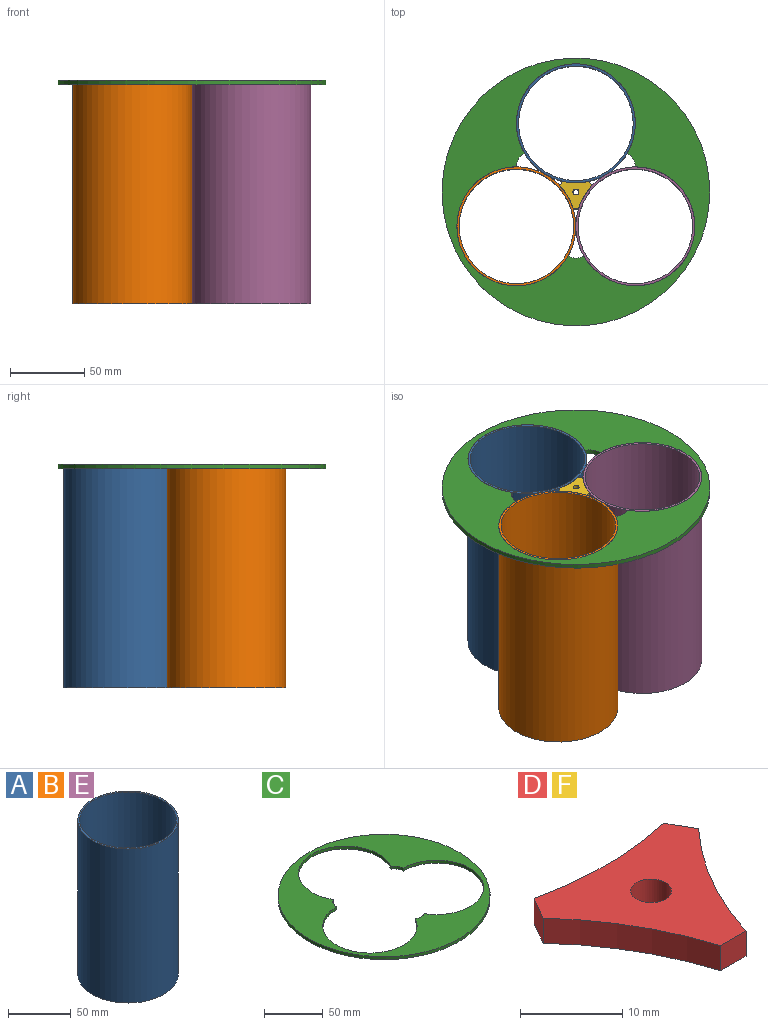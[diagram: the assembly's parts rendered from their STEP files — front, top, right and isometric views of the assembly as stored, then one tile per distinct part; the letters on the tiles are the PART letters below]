
ASSEMBLY  parts=6 mates=11
PART A: 4 faces, bbox 80x80x150 mm
  f0: cylinder r=38.5mm len=150mm, axis (0,0,-1), area 36285.4mm2, adj f2,f3
  f1: cylinder r=40mm len=150mm, axis (0,0,-1), area 37699.1mm2, adj f2,f3
  f2: plane 80x80mm, normal (0,0,1), area 369.9mm2, adj f0,f1
  f3: plane 80x80mm, normal (0,0,-1), area 369.9mm2, adj f0,f1
PART B: same geometry as A
PART C: 9 faces, bbox 180x180x3 mm
  f0: cylinder r=40mm len=80mm, axis (0,0,-1), area 502.7mm2, adj f1,f5,f7,f8
  f1: cylinder r=10.72mm len=9.28mm, axis (0,0,-1), area 33.7mm2, adj f0,f2,f7,f8
  f2: cylinder r=40mm len=80mm, axis (0,0,-1), area 502.7mm2, adj f1,f3,f7,f8
  f3: cylinder r=10.72mm len=10.72mm, axis (0,0,-1), area 33.7mm2, adj f2,f4,f7,f8
  f4: cylinder r=40mm len=80mm, axis (0,0,-1), area 502.7mm2, adj f3,f5,f7,f8
  f5: cylinder r=10.72mm len=9.28mm, axis (0,0,-1), area 33.7mm2, adj f0,f4,f7,f8
  f6: cylinder r=90mm len=180mm, axis (0,0,-1), area 1696.5mm2, adj f7,f8
  f7: plane 180x180mm, normal (0,0,1), area 9869.8mm2, adj f0,f1,f2,f3,f4,f5,f6
  f8: plane 180x180mm, normal (0,0,-1), area 9869.8mm2, adj f0,f1,f2,f3,f4,f5,f6
PART D: 9 faces, bbox 21.5x18.6x3 mm
  f0: plane 3.03x3mm, normal (-0.87,0.5,0), area 10.5mm2, adj f1,f5,f7,f8
  f1: cylinder r=40mm len=15.57mm, axis (0,0,-1), area 54.4mm2, adj f0,f2,f7,f8
  f2: plane 3.5x3mm, normal (0,-1,0), area 10.5mm2, adj f1,f3,f7,f8
  f3: cylinder r=40mm len=15.57mm, axis (0,0,-1), area 54.4mm2, adj f2,f4,f7,f8
  f4: plane 3.03x3mm, normal (0.87,0.5,0), area 10.5mm2, adj f3,f5,f7,f8
  f5: cylinder r=40mm len=17.98mm, axis (0,0,-1), area 54.4mm2, adj f0,f4,f7,f8
  f6: cylinder r=2mm len=4mm, axis (0,0,-1), area 37.7mm2, adj f7,f8
  f7: plane 21.48x18.6mm, normal (0,0,1), area 204.8mm2, adj f0,f1,f2,f3,f4,f5,f6
  f8: plane 21.48x18.6mm, normal (0,0,-1), area 204.8mm2, adj f0,f1,f2,f3,f4,f5,f6
PART E: same geometry as A
PART F: same geometry as D
PLACE A t=(-96.12,239.6,81.35)mm
PLACE B rot(axis=(0,0,-1),90deg) t=(-136.12,170.32,81.35)mm
PLACE C t=(-136.12,170.32,228.35)mm
PLACE D t=(-136.12,170.32,81.35)mm
PLACE E t=(-56.12,170.32,81.35)mm
PLACE F t=(-136.12,170.32,228.35)mm
MATE slider F.f3 <-> E.f1  axis (0,0,-1) through (-56.12,170.32,229.85)mm
MATE fastened A.f1 <-> C.f0  axis (0,0,1) through (-96.12,239.6,231.35)mm
MATE cylindrical A.f1 <-> C.f0  axis (0,0,1) through (-96.12,239.6,231.35)mm
MATE fastened F.f1 <-> B.f1  axis (0,0,1) through (-136.12,170.32,231.35)mm
MATE cylindrical E.f1 <-> C.f2  axis (0,0,1) through (-56.12,170.32,231.35)mm
MATE cylindrical F.f1 <-> B.f1  axis (0,0,-1) through (-136.12,170.32,229.85)mm
MATE fastened D.f3 <-> E.f1  axis (0,0,-1) through (-56.12,170.32,81.35)mm
MATE cylindrical C.f4 <-> B.f0  axis (0,0,-1) through (-136.12,170.32,228.35)mm
MATE fastened B.f1 <-> C.f4  axis (0,0,1) through (-136.12,170.32,231.35)mm
MATE cylindrical D.f1 <-> B.f1  axis (0,0,-1) through (-136.12,170.32,82.85)mm
MATE fastened E.f1 <-> C.f2  axis (0,0,1) through (-56.12,170.32,231.35)mm
